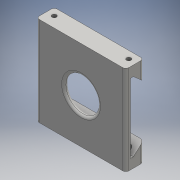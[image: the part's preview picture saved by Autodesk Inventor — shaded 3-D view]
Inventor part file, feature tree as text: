
AUTODESK INVENTOR PART (.ipt)
format: ipt  version: 2016 (Build 200138000, 138)  size: 197,120 bytes
history: native  units: mm
features: extrude x4, sketch x4, fillet x3
ambient origin geometry x8: Origin, YZ Plane, XZ Plane, XY Plane, X Axis, Y Axis, Z Axis, Center Point
bodies: Solid1 (feature_tree)
feature tree (11):
  extrude  "Block"  Depth=60.0mm
  extrude  "Tripod Slot"  Depth=5.0mm
  extrude  "Plastic Thinning"  Depth=5.0mm
  fillet  "Strength"  Radius=5.0mm
  fillet  "Fillet3"  Radius=5.0mm
  extrude  "Extrusion4"  Depth=2.0mm
  fillet  "Fillet4"  Radius=3.0mm
  sketch  "Sketch1"  dims[d0=60.0mm d1=60.0mm]
  sketch  "Sketch2"  dims[d2=5.0mm d3=5.0mm]
  sketch  "Sketch3"  dims[d4=5.0mm d5=5.0mm d6=5.0mm d7=5.0mm]
  sketch  "Sketch4"  dims[d8=5.0mm d9=5.0mm d10=3.0mm d11=3.0mm d12=3.0mm d13=3.0mm d14=60.0mm d15=0.0mm d17=17.25mm d18=17.25mm d19=8.9mm d20=23.25mm d21=23.25mm d22=2.0mm d23=2.0mm d24=60.0mm d25=0.0mm d26=5.0mm d27=90.0deg d28=5.0mm d29=90.0deg d30=7.5mm d31=90.0deg d32=7.5mm d33=90.0deg d34=25.0mm d35=25.0mm d36=25.0mm d37=25.0mm d38=90.0deg d39=90.0deg d40=4.861193mm d41=4.861193mm d42=55.0mm d43=60.0mm d44=0.0mm d45=3.0mm d46=12.0mm d47=2.0mm d48=22.5mm d49=12.25mm d50=0.0mm d51=2.0mm]
